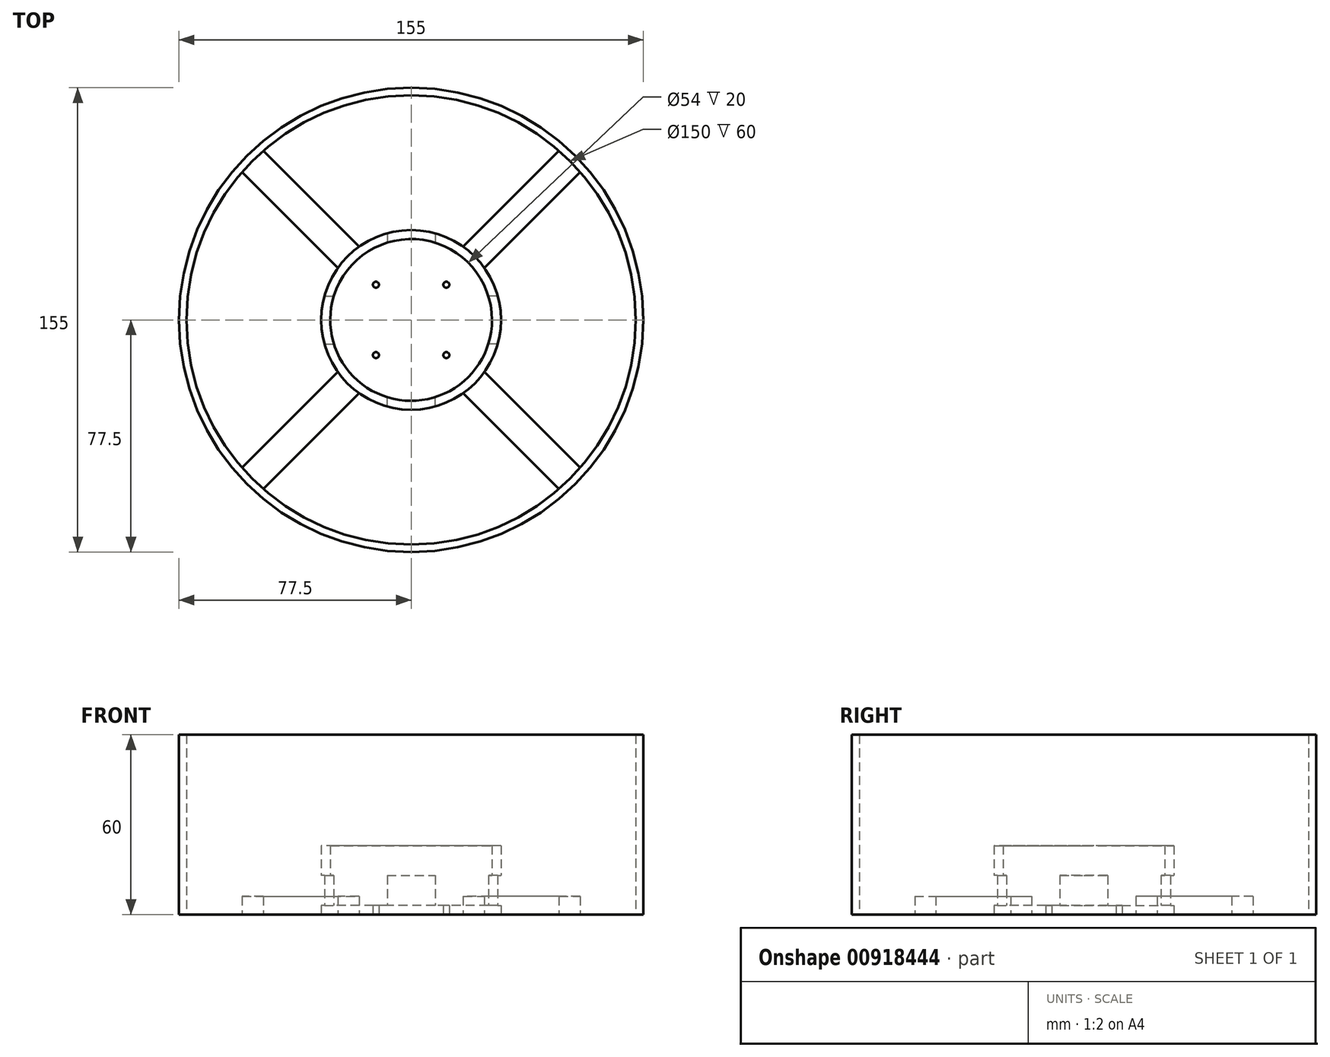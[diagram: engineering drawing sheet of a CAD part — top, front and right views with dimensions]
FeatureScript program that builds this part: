
annotation { "Feature Type Name" : "Feature", "Feature Type Description" : "" }
export const myFeature = defineFeature(function(context is Context, id is Id, definition is map)
    precondition{}
    {
        {
            var Q0;
            Q0=qCreatedBy(makeId("Top.planeOp"),FACE);
            var sketch = newSketch(context, id + "F0", { "sketchPlane" : qUnion([Q0])});
            skCircle(sketch, "E0", {"center": v(0, 0) * mm, "radius": 77.5 * mm});
            skCircle(sketch, "E1", {"center": v(0, 0) * mm, "radius": 75 * mm});
            skSolve(sketch);
        }
        {
            var Q0;
            Q0 = qSketchRegion(id + "F0", true);
            var Q1;
            Q1=makeQuery(id+"F0.imprint","IMPRINT",FACE,{"disambiguationData":[TD([[makeQuery(id+"F0.imprint","IMPRINT",EDGE,{"derivedFrom":sQuery(id+"F0.wireOp",EDGE,"E0")}),1.0]])]});
            extrude(context, id + "F1", {"entities" : qUnion([Q0, Q1]), "depth" : 60 * mm, "offsetDistance" : 25 * mm});
        }
        {
            var Q0;
            Q0=qCreatedBy(makeId("Top.planeOp"),FACE);
            var sketch = newSketch(context, id + "F2", { "sketchPlane" : qUnion([Q0])});
            skPoint(sketch, "E2.middle", {"position": v(0, 0) * mm});
            skCircle(sketch, "E3", {"center": v(11.75, -11.75) * mm, "radius": 1 * mm});
            skCircle(sketch, "E4.0.1.0", {"center": v(11.75, 11.75) * mm, "radius": 1 * mm});
            skCircle(sketch, "E4.1.0.0", {"center": v(-11.75, -11.75) * mm, "radius": 1 * mm});
            skCircle(sketch, "E4.1.1.0", {"center": v(-11.75, 11.75) * mm, "radius": 1 * mm});
            skLineSegment(sketch, "E4.direction1", {"start": v(11.75, -11.75) * mm, "end": v(-11.75, -11.75) * mm, "construction": true});
            skLineSegment(sketch, "E4.direction2", {"start": v(11.75, -11.75) * mm, "end": v(11.75, 11.75) * mm, "construction": true});
            skCircle(sketch, "E5", {"center": v(0, 0) * mm, "radius": 30 * mm});
            skSolve(sketch);
        }
        {
            var Q0;
            Q0 = qSketchRegion(id + "F2", true);
            extrude(context, id + "F3", {"entities" : qUnion([Q0]), "depth" : 3 * mm, "offsetDistance" : 25 * mm});
        }
        {
            var Q0;
            Q0=qCreatedBy(makeId("Top.planeOp"),FACE);
            cPlane(context, id + "F4", {"entities" : qUnion([Q0]), "cplaneType" : CPlaneType.OFFSET, "offset" : 3 * mm, "width" : 150 * mm, "height" : 150 * mm});
        }
        {
            var Q0;
            Q0=qCreatedBy(id+"F4.planeOp",FACE);
            var sketch = newSketch(context, id + "F5", { "sketchPlane" : qUnion([Q0])});
            skArc(sketch, "E6", {"start": v(-26.02, -7.2) * mm, "mid": v(-19.38, -18.8) * mm, "end": v(-8, -25.79) * mm});
            skArc(sketch, "E7.0", {"start": v(-28.91, -8) * mm, "mid": v(-21.21, -21.21) * mm, "end": v(-8, -28.91) * mm});
            skLineSegment(sketch, "E8", {"start": v(-28.91, 8) * mm, "end": v(-25.79, 8) * mm});
            skLineSegment(sketch, "E9", {"start": v(-28.91, -8) * mm, "end": v(-25.79, -8) * mm});
            skLineSegment(sketch, "E10.1.0", {"start": v(8, 28.91) * mm, "end": v(8, 25.79) * mm});
            skLineSegment(sketch, "E10.1.1", {"start": v(-8, 28.91) * mm, "end": v(-8, 25.79) * mm});
            skLineSegment(sketch, "E10.2.0", {"start": v(28.91, -8) * mm, "end": v(25.79, -8) * mm});
            skLineSegment(sketch, "E10.2.1", {"start": v(28.91, 8) * mm, "end": v(25.79, 8) * mm});
            skLineSegment(sketch, "E10.3.0", {"start": v(-8, -28.91) * mm, "end": v(-8, -25.79) * mm});
            skLineSegment(sketch, "E10.3.1", {"start": v(8, -28.91) * mm, "end": v(8, -25.79) * mm});
            skLineSegment(sketch, "E10.anchor1", {"start": v(0, 0) * mm, "end": v(-28.91, -8) * mm, "construction": true});
            skLineSegment(sketch, "E10.anchor2", {"start": v(0, 0) * mm, "end": v(8, -28.91) * mm, "construction": true});
            skArc(sketch, "E11.trimOffspring", {"start": v(-8, 25.79) * mm, "mid": v(-19.1, 19.1) * mm, "end": v(-25.79, 8) * mm});
            skArc(sketch, "E12.trimOffspring", {"start": v(-8, 28.91) * mm, "mid": v(-21.21, 21.21) * mm, "end": v(-28.91, 8) * mm});
            skArc(sketch, "E13.trimOffspring", {"start": v(28.91, 8) * mm, "mid": v(21.21, 21.21) * mm, "end": v(8, 28.91) * mm});
            skArc(sketch, "E14.trimOffspring", {"start": v(25.79, 8) * mm, "mid": v(19.1, 19.1) * mm, "end": v(8, 25.79) * mm});
            skArc(sketch, "E15.trimOffspring", {"start": v(7.2, -26.02) * mm, "mid": v(18.8, -19.38) * mm, "end": v(25.79, -8) * mm});
            skArc(sketch, "E16.trimOffspring", {"start": v(8, -28.91) * mm, "mid": v(21.21, -21.21) * mm, "end": v(28.91, -8) * mm});
            skSolve(sketch);
        }
        {
            var Q0;
            Q0 = qSketchRegion(id + "F5", true);
            extrude(context, id + "F6", {"entities" : qUnion([Q0]), "operationType" : NewBodyOperationType.ADD, "depth" : 10 * mm, "offsetDistance" : 25 * mm});
        }
        {
            var Q0;
            Q0=makeQuery(id+"F6.opExtrude","CAP_FACE",FACE,{"disambiguationData":[OSD([sQuery(id+"F5.wireOp",EDGE,"E8"),sQuery(id+"F5.wireOp",EDGE,"E10.1.1"),sQuery(id+"F5.wireOp",EDGE,"E11.trimOffspring"),sQuery(id+"F5.wireOp",EDGE,"E12.trimOffspring")])],"isStart":false});
            cPlane(context, id + "F7", {"entities" : qUnion([Q0]), "cplaneType" : CPlaneType.OFFSET, "offset" : 0 * mm, "width" : 150 * mm, "height" : 150 * mm});
        }
        {
            var Q0;
            Q0=qCreatedBy(id+"F7.planeOp",FACE);
            var sketch = newSketch(context, id + "F8", { "sketchPlane" : qUnion([Q0])});
            skCircle(sketch, "E17", {"center": v(0, 0) * mm, "radius": 30 * mm});
            skCircle(sketch, "E18.0", {"center": v(0, 0) * mm, "radius": 27 * mm});
            skSolve(sketch);
        }
        {
            var Q0;
            Q0=makeQuery(id+"F8.imprint","IMPRINT",FACE,{"disambiguationData":[TD([[makeQuery(id+"F8.imprint","IMPRINT",EDGE,{"derivedFrom":sQuery(id+"F8.wireOp",EDGE,"E17")}),1.0]])]});
            extrude(context, id + "F9", {"entities" : qUnion([Q0]), "operationType" : NewBodyOperationType.ADD, "depth" : 10 * mm, "offsetDistance" : 25 * mm});
        }
        {
            var Q0;
            Q0=qCreatedBy(makeId("Top.planeOp"),FACE);
            var sketch = newSketch(context, id + "F10", { "sketchPlane" : qUnion([Q0])});
            skArc(sketch, "E19", {"start": v(-24.45, -17.38) * mm, "mid": v(-21.21, -21.21) * mm, "end": v(-17.38, -24.45) * mm});
            skArc(sketch, "E20", {"start": v(-56.45, -49.38) * mm, "mid": v(-53.03, -53.03) * mm, "end": v(-49.38, -56.45) * mm});
            skLineSegment(sketch, "E21", {"start": v(-49.38, -56.45) * mm, "end": v(-17.38, -24.45) * mm});
            skLineSegment(sketch, "E22.MirrorCS", {"start": v(-56.45, -49.38) * mm, "end": v(-24.45, -17.38) * mm});
            skLineSegment(sketch, "E23.1.0", {"start": v(56.45, -49.38) * mm, "end": v(24.45, -17.38) * mm});
            skLineSegment(sketch, "E23.1.1", {"start": v(49.38, -56.45) * mm, "end": v(17.38, -24.45) * mm});
            skArc(sketch, "E23.1.2", {"start": v(17.38, -24.45) * mm, "mid": v(21.21, -21.21) * mm, "end": v(24.45, -17.38) * mm});
            skArc(sketch, "E23.1.3", {"start": v(49.38, -56.45) * mm, "mid": v(53.03, -53.03) * mm, "end": v(56.45, -49.38) * mm});
            skLineSegment(sketch, "E23.2.0", {"start": v(49.38, 56.45) * mm, "end": v(17.38, 24.45) * mm});
            skLineSegment(sketch, "E23.2.1", {"start": v(56.45, 49.38) * mm, "end": v(24.45, 17.38) * mm});
            skArc(sketch, "E23.2.2", {"start": v(24.45, 17.38) * mm, "mid": v(21.21, 21.21) * mm, "end": v(17.38, 24.45) * mm});
            skArc(sketch, "E23.2.3", {"start": v(56.45, 49.38) * mm, "mid": v(53.03, 53.03) * mm, "end": v(49.38, 56.45) * mm});
            skLineSegment(sketch, "E23.3.0", {"start": v(-56.45, 49.38) * mm, "end": v(-24.45, 17.38) * mm});
            skLineSegment(sketch, "E23.3.1", {"start": v(-49.38, 56.45) * mm, "end": v(-17.38, 24.45) * mm});
            skArc(sketch, "E23.3.2", {"start": v(-17.38, 24.45) * mm, "mid": v(-21.21, 21.21) * mm, "end": v(-24.45, 17.38) * mm});
            skArc(sketch, "E23.3.3", {"start": v(-49.38, 56.45) * mm, "mid": v(-53.03, 53.03) * mm, "end": v(-56.45, 49.38) * mm});
            skLineSegment(sketch, "E23.anchor1", {"start": v(0, 0) * mm, "end": v(-49.38, -56.45) * mm, "construction": true});
            skLineSegment(sketch, "E23.anchor2", {"start": v(0, 0) * mm, "end": v(-56.45, 49.38) * mm, "construction": true});
            skSolve(sketch);
        }
        {
            var Q0;
            Q0 = qSketchRegion(id + "F10", true);
            extrude(context, id + "F11", {"entities" : qUnion([Q0]), "depth" : 6 * mm, "offsetDistance" : 25 * mm});
        }
    });
